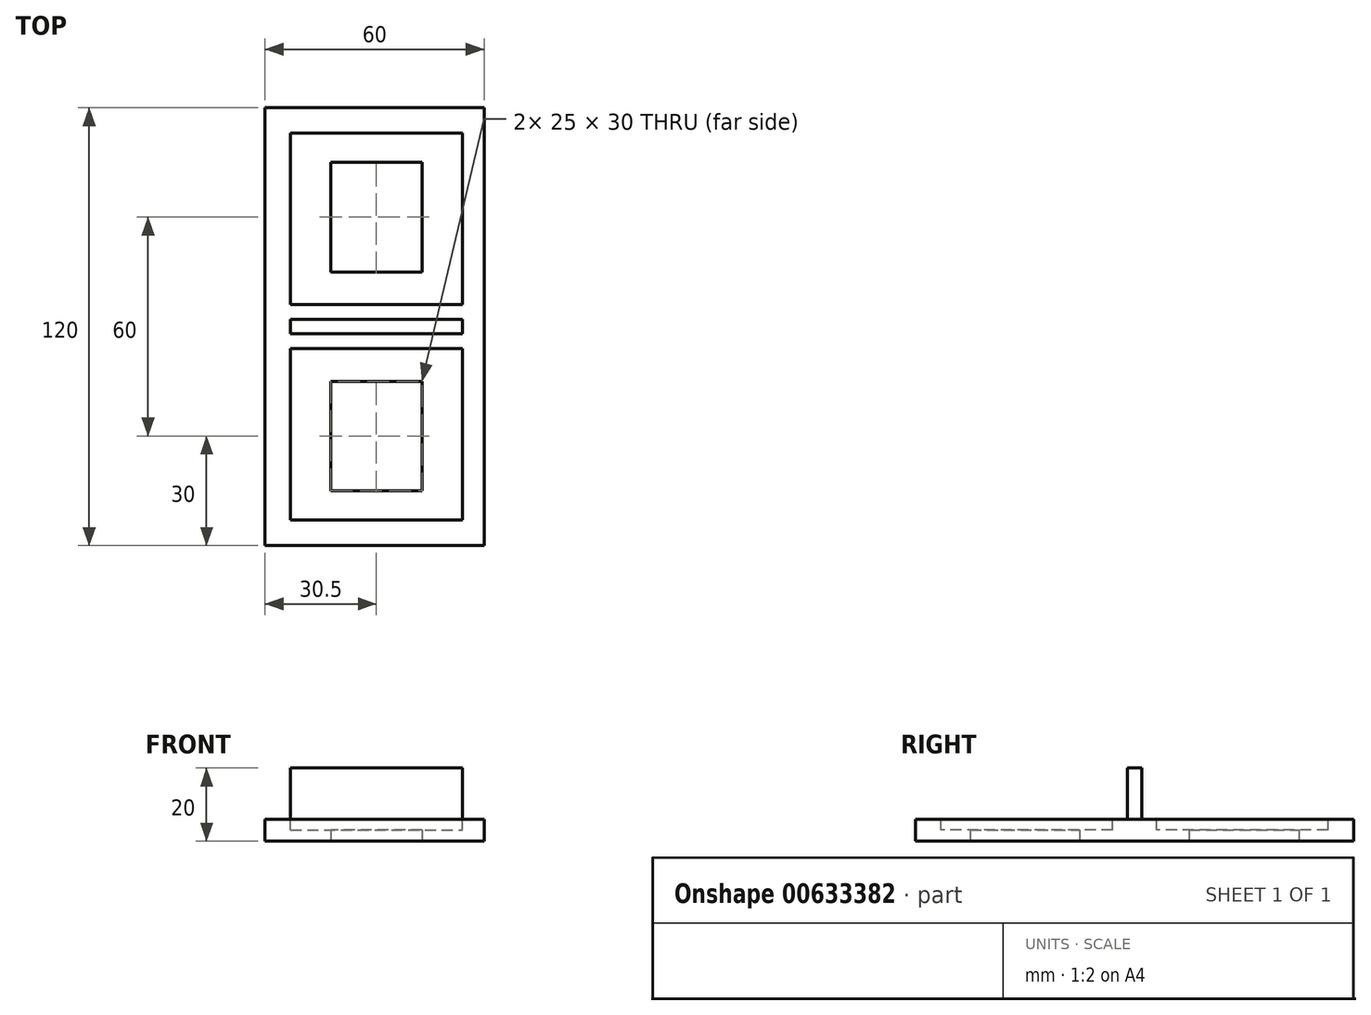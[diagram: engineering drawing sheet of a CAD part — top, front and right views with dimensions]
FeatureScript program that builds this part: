
annotation { "Feature Type Name" : "Feature", "Feature Type Description" : "" }
export const myFeature = defineFeature(function(context is Context, id is Id, definition is map)
    precondition{}
    {
        {
            var Q0;
            Q0=qCreatedBy(makeId("Top.planeOp"),FACE);
            var sketch = newSketch(context, id + "F0", { "sketchPlane" : qUnion([Q0])});
            skLineSegment(sketch, "E0.bottom", {"start": v(0, 120) * mm, "end": v(60, 120) * mm});
            skLineSegment(sketch, "E0.top", {"start": v(0, 0) * mm, "end": v(60, 0) * mm});
            skLineSegment(sketch, "E0.left", {"start": v(0, 120) * mm, "end": v(0, 0) * mm});
            skLineSegment(sketch, "E0.right", {"start": v(60, 120) * mm, "end": v(60, 0) * mm});
            skPoint(sketch, "E1", {"position": v(0, 0) * mm});
            skPoint(sketch, "E2", {"position": v(60, 0) * mm});
            skPoint(sketch, "E3", {"position": v(60, 120) * mm});
            skPoint(sketch, "E4", {"position": v(0, 120) * mm});
            skLineSegment(sketch, "E5.top", {"start": v(0, 60) * mm, "end": v(60, 60) * mm});
            skLineSegment(sketch, "E5.left", {"start": v(0, 120) * mm, "end": v(0, 60) * mm});
            skLineSegment(sketch, "E5.right", {"start": v(60, 120) * mm, "end": v(60, 60) * mm});
            skSolve(sketch);
        }
        {
            var Q0;
            Q0 = qSketchRegion(id + "F0", true);
            extrude(context, id + "F1", {"entities" : qUnion([Q0]), "depth" : 6 * mm, "offsetDistance" : 25 * mm});
        }
        {
            var Q0;
            Q0=makeQuery(id+"F1.opExtrude","CAP_FACE",FACE,{"disambiguationData":[OSD([sQuery(id+"F0.wireOp",EDGE,"E0.top"),sQuery(id+"F0.wireOp",EDGE,"E0.left"),sQuery(id+"F0.wireOp",EDGE,"E0.right"),sQuery(id+"F0.wireOp",EDGE,"E0.bottom"),sQuery(id+"F0.wireOp",EDGE,"E5.left"),sQuery(id+"F0.wireOp",EDGE,"E5.right")])],"isStart":false});
            var sketch = newSketch(context, id + "F2", { "sketchPlane" : qUnion([Q0])});
            skLineSegment(sketch, "E6.bottom", {"start": v(7, 113) * mm, "end": v(54, 113) * mm});
            skLineSegment(sketch, "E6.top", {"start": v(7, 66) * mm, "end": v(54, 66) * mm});
            skLineSegment(sketch, "E6.left", {"start": v(7, 113) * mm, "end": v(7, 66) * mm});
            skLineSegment(sketch, "E6.right", {"start": v(54, 113) * mm, "end": v(54, 66) * mm});
            skLineSegment(sketch, "E7.bottom", {"start": v(7, 54) * mm, "end": v(54, 54) * mm});
            skLineSegment(sketch, "E7.top", {"start": v(7, 7) * mm, "end": v(54, 7) * mm});
            skLineSegment(sketch, "E7.left", {"start": v(7, 54) * mm, "end": v(7, 7) * mm});
            skLineSegment(sketch, "E7.right", {"start": v(54, 54) * mm, "end": v(54, 7) * mm});
            skSolve(sketch);
        }
        {
            var Q0;
            Q0 = qSketchRegion(id + "F2", true);
            extrude(context, id + "F3", {"entities" : qUnion([Q0]), "operationType" : NewBodyOperationType.REMOVE, "oppositeDirection" : true, "depth" : 3 * mm, "offsetDistance" : 25 * mm});
        }
        {
            var Q0;
            Q0=qCreatedBy(makeId("Top.planeOp"),FACE);
            var sketch = newSketch(context, id + "F4", { "sketchPlane" : qUnion([Q0])});
            skLineSegment(sketch, "E8.bottom", {"start": v(7, 62) * mm, "end": v(54, 62) * mm});
            skLineSegment(sketch, "E8.top", {"start": v(7, 58) * mm, "end": v(54, 58) * mm});
            skLineSegment(sketch, "E8.left", {"start": v(7, 62) * mm, "end": v(7, 58) * mm});
            skLineSegment(sketch, "E8.right", {"start": v(54, 62) * mm, "end": v(54, 58) * mm});
            skSolve(sketch);
        }
        {
            var Q0;
            Q0 = qSketchRegion(id + "F4", true);
            extrude(context, id + "F5", {"entities" : qUnion([Q0]), "operationType" : NewBodyOperationType.ADD, "depth" : 20 * mm, "offsetDistance" : 25 * mm});
        }
        {
            var Q0;
            Q0=qCreatedBy(makeId("Top.planeOp"),FACE);
            var sketch = newSketch(context, id + "F6", { "sketchPlane" : qUnion([Q0])});
            skLineSegment(sketch, "E9.bottom", {"start": v(18, 45) * mm, "end": v(43, 45) * mm});
            skLineSegment(sketch, "E9.top", {"start": v(18, 15) * mm, "end": v(43, 15) * mm});
            skLineSegment(sketch, "E9.left", {"start": v(18, 45) * mm, "end": v(18, 15) * mm});
            skLineSegment(sketch, "E9.right", {"start": v(43, 45) * mm, "end": v(43, 15) * mm});
            skLineSegment(sketch, "E10.bottom", {"start": v(18, 105) * mm, "end": v(43, 105) * mm});
            skLineSegment(sketch, "E10.top", {"start": v(18, 75) * mm, "end": v(43, 75) * mm});
            skLineSegment(sketch, "E10.left", {"start": v(18, 105) * mm, "end": v(18, 75) * mm});
            skLineSegment(sketch, "E10.right", {"start": v(43, 105) * mm, "end": v(43, 75) * mm});
            skSolve(sketch);
        }
        {
            var Q0;
            Q0 = qSketchRegion(id + "F6", true);
            extrude(context, id + "F7", {"entities" : qUnion([Q0]), "operationType" : NewBodyOperationType.REMOVE, "depth" : 25 * mm, "offsetDistance" : 25 * mm});
        }
    });
